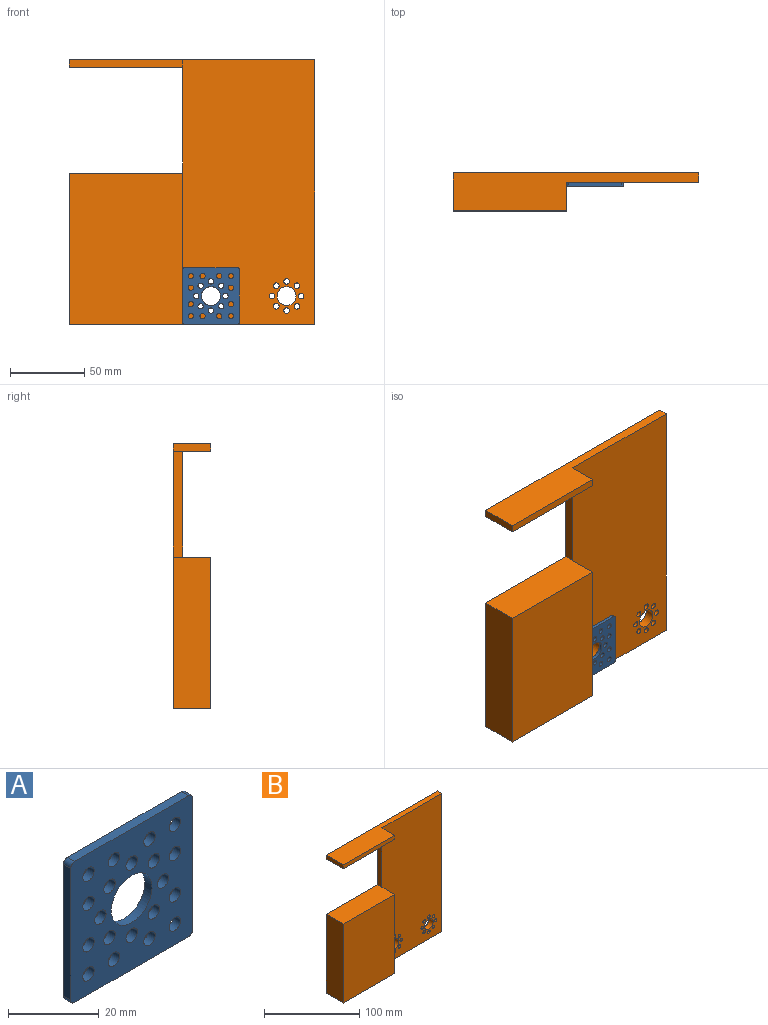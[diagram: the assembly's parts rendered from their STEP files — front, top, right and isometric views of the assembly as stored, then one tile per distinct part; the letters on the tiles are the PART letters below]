
ASSEMBLY  parts=2 mates=1
PART A: 31 faces, bbox 38.1x2.3x38.1 mm
  f0: cylinder r=1.78mm len=3.56mm, axis (0,1,0), area 25.5mm2, adj f21,f22
  f1: cylinder r=1.78mm len=3.56mm, axis (0,1,0), area 25.5mm2, adj f21,f22
  f2: cylinder r=1.78mm len=3.56mm, axis (0,1,0), area 25.5mm2, adj f21,f22
  f3: cylinder r=1.78mm len=3.56mm, axis (0,1,0), area 25.5mm2, adj f21,f22
  f4: cylinder r=1.78mm len=3.56mm, axis (0,1,0), area 25.5mm2, adj f21,f22
  f5: cylinder r=1.78mm len=3.56mm, axis (0,1,0), area 25.5mm2, adj f21,f22
  f6: cylinder r=1.78mm len=3.56mm, axis (0,1,0), area 25.5mm2, adj f21,f22
  f7: cylinder r=1.78mm len=3.56mm, axis (0,1,0), area 25.5mm2, adj f21,f22
  f8: cylinder r=1.78mm len=3.56mm, axis (0,1,0), area 25.5mm2, adj f21,f22
  f9: cylinder r=1.78mm len=3.56mm, axis (0,1,0), area 25.5mm2, adj f21,f22
  f10: cylinder r=1.78mm len=3.56mm, axis (0,1,0), area 25.5mm2, adj f21,f22
  f11: cylinder r=1.78mm len=3.56mm, axis (0,1,0), area 25.5mm2, adj f21,f22
  f12: cylinder r=1.78mm len=3.56mm, axis (0,1,0), area 25.5mm2, adj f21,f22
  f13: cylinder r=1.78mm len=3.56mm, axis (0,1,0), area 25.5mm2, adj f21,f22
  f14: cylinder r=1.78mm len=3.56mm, axis (0,1,0), area 25.5mm2, adj f21,f22
  f15: cylinder r=1.78mm len=3.56mm, axis (0,1,0), area 25.5mm2, adj f21,f22
  f16: cylinder r=1.78mm len=3.56mm, axis (0,1,0), area 25.5mm2, adj f21,f22
  f17: cylinder r=1.78mm len=3.56mm, axis (0,1,0), area 25.5mm2, adj f21,f22
  f18: cylinder r=1.78mm len=3.56mm, axis (0,1,0), area 25.5mm2, adj f21,f22
  f19: cylinder r=1.78mm len=3.56mm, axis (0,1,0), area 25.5mm2, adj f21,f22
  f20: cylinder r=6.36mm len=12.73mm, axis (0,1,0), area 91.4mm2, adj f21,f22
  f21: plane 38.1x38.1mm, normal (0,1,0), area 1124.4mm2, adj f0,f1,f2,f3,f4,f5,f6,f7
  f22: plane 38.1x38.1mm, normal (0,-1,0), area 1124.4mm2, adj f0,f1,f2,f3,f4,f5,f6,f7
  f23: plane 35.56x2.29mm, normal (1,0,0), area 81.3mm2, adj f21,f22,f27,f29
  f24: plane 35.56x2.29mm, normal (0,0,-1), area 81.3mm2, adj f21,f22,f29,f30
  f25: plane 35.56x2.29mm, normal (-1,0,0), area 81.3mm2, adj f21,f22,f28,f30
  f26: plane 35.56x2.29mm, normal (0,0,1), area 81.3mm2, adj f21,f22,f27,f28
  f27: cylinder r=1.27mm len=2.29mm, axis (0,-1,0), area 4.6mm2, adj f21,f22,f23,f26
  f28: cylinder r=1.27mm len=2.29mm, axis (0,-1,0), area 4.6mm2, adj f21,f22,f25,f26
  f29: cylinder r=1.27mm len=2.29mm, axis (0,-1,0), area 4.6mm2, adj f21,f22,f23,f24
  f30: cylinder r=1.27mm len=2.29mm, axis (0,-1,0), area 4.6mm2, adj f21,f22,f24,f25
PART B: 32 faces, bbox 165.1x25.4x177.8 mm
  f0: plane 71.12x6.35mm, normal (-1,0,0), area 451.6mm2, adj f22,f23,f25,f30
  f1: plane 165.1x25.4mm, normal (0,0,-1), area 2500mm2, adj f2,f22,f23,f24,f26,f27
  f2: plane 177.8x6.35mm, normal (1,0,0), area 1129mm2, adj f1,f21,f22,f23
  f3: cylinder r=1.9mm len=6.35mm, axis (0,1,0), area 75.8mm2, adj f22,f23
  f4: cylinder r=1.9mm len=6.35mm, axis (0,1,0), area 75.8mm2, adj f22,f23
  f5: cylinder r=1.9mm len=6.35mm, axis (0,1,0), area 75.8mm2, adj f22,f23
  f6: cylinder r=1.9mm len=6.35mm, axis (0,1,0), area 75.8mm2, adj f22,f23
  f7: cylinder r=1.9mm len=6.35mm, axis (0,1,0), area 75.8mm2, adj f22,f23
  f8: cylinder r=1.9mm len=6.35mm, axis (0,1,0), area 75.8mm2, adj f22,f23
  f9: cylinder r=1.9mm len=6.35mm, axis (0,1,0), area 75.8mm2, adj f22,f23
  f10: cylinder r=1.9mm len=6.35mm, axis (0,1,0), area 75.8mm2, adj f22,f23
  f11: cylinder r=1.9mm len=6.35mm, axis (0,1,0), area 75.8mm2, adj f22,f23
  f12: cylinder r=1.9mm len=6.35mm, axis (0,1,0), area 75.8mm2, adj f22,f23
  f13: cylinder r=1.9mm len=6.35mm, axis (0,1,0), area 75.8mm2, adj f22,f23
  f14: cylinder r=1.9mm len=6.35mm, axis (0,1,0), area 75.8mm2, adj f22,f23
  f15: cylinder r=1.9mm len=6.35mm, axis (0,1,0), area 75.8mm2, adj f22,f23
  f16: cylinder r=1.9mm len=6.35mm, axis (0,1,0), area 75.8mm2, adj f22,f23
  f17: cylinder r=1.9mm len=6.35mm, axis (0,1,0), area 75.8mm2, adj f22,f23
  f18: cylinder r=1.9mm len=6.35mm, axis (0,1,0), area 75.8mm2, adj f22,f23
  f19: cylinder r=6.35mm len=12.7mm, axis (0,1,0), area 253.4mm2, adj f22,f23
  f20: cylinder r=6.35mm len=12.7mm, axis (0,1,0), area 253.4mm2, adj f22,f23
  f21: plane 165.1x25.4mm, normal (0,0,1), area 2500mm2, adj f2,f22,f23,f28,f29,f31
  f22: plane 177.8x88.9mm, normal (0,-1,0), area 15371.6mm2, adj f0,f1,f2,f3,f4,f5,f6,f7
  f23: plane 177.8x165.1mm, normal (0,1,0), area 23500.6mm2, adj f0,f1,f2,f3,f4,f5,f6,f7
  f24: plane 101.6x19.05mm, normal (1,0,0), area 1935.5mm2, adj f1,f22,f25,f27
  f25: plane 76.2x25.4mm, normal (0,0,1), area 1935.5mm2, adj f0,f23,f24,f26,f27
  f26: plane 101.6x25.4mm, normal (-1,0,0), area 2580.6mm2, adj f1,f23,f25,f27
  f27: plane 101.6x76.2mm, normal (0,-1,0), area 7741.9mm2, adj f1,f24,f25,f26
  f28: plane 19.05x5.08mm, normal (1,0,0), area 96.8mm2, adj f21,f22,f30,f31
  f29: plane 25.4x5.08mm, normal (-1,0,0), area 129mm2, adj f21,f23,f30,f31
  f30: plane 76.2x25.4mm, normal (0,0,-1), area 1935.5mm2, adj f0,f23,f28,f29,f31
  f31: plane 76.2x5.08mm, normal (0,-1,0), area 387.1mm2, adj f21,f28,f29,f30
PLACE A t=(-46.59,26.67,-3.31)mm
PLACE B t=(-116.44,35.3,-22.36)mm
MATE fastened A.f20 <-> B.f19  axis (0,1,0) through (-46.59,28.95,-3.31)mm
